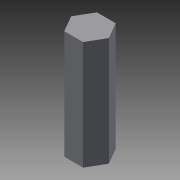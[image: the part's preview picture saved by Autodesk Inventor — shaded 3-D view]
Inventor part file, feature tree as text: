
AUTODESK INVENTOR PART (.ipt)
format: ipt  version: 2013 (Build 170138000, 138)  size: 68,608 bytes
history: native  units: in
note: dims shown in document units (in); Inventor stores cm internally (conversion verified against a paired STEP export)
features: extrude x1, sketch x1
ambient origin geometry x8: Origin, YZ Plane, XZ Plane, XY Plane, X Axis, Y Axis, Z Axis, Center Point
bodies: Solid1 (feature_tree)
feature tree (2):
  extrude  "Extrusion1"  Depth=1.25in TaperAngle=0.0deg
  sketch  "Sketch1"  dims[d0=0.375in d1=1.25in d2=0.0in]
